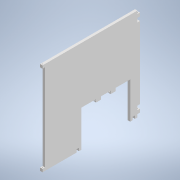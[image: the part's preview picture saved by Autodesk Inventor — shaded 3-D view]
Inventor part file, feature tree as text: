
AUTODESK INVENTOR PART (.ipt)
format: ipt  version: 2020 (Build 240168000, 168)  size: 333,312 bytes
history: native  units: in
note: dims shown in document units (in); Inventor stores cm internally (conversion verified against a paired STEP export)
features: sketch x9, hole x7, extrude x6, shell x1, fillet x1, plane x1, split x1
ambient origin geometry x8: Origin, YZ Plane, XZ Plane, XY Plane, X Axis, Y Axis, Z Axis, Center Point
bodies: Solid1 (feature_tree)
feature tree (26):
  extrude  "Extrusion1"  Depth=7.874in
  shell  "Shell1"  Thickness=7.874in
  extrude  "Extrusion2"  Depth=1.6339in
  sketch  "Sketch3"  dims[d7=6.1024in d8=1.6339in]
  extrude  "Extrusion3"  Depth=1.5748in
  hole  "Hole1"  [1 undecoded]
  fillet  "Fillet2"  Radius=0.8661in
  extrude  "Extrusion4"  Depth=1.1417in
  plane  "Work Plane3"
  split  "Split1"
  extrude  "Extrusion11"  Depth=0.3937in
  hole  "Hole3"  [1 undecoded]
  hole  "Hole4"  [1 undecoded]
  hole  "Hole5"  [1 undecoded]
  hole  "Hole6"  [1 undecoded]
  extrude  "Extrusion12"  Depth=0.3937in
  hole  "Hole7"  [1 undecoded]
  sketch  "Sketch1"  dims[d0=7.874in d1=7.874in d2=7.874in d3=0.0in]
  sketch  "Sketch6"  dims[d9=0.3937in d10=0.0in d12=1.5748in]
  sketch  "Sketch7"  dims[d13=1.5748in d16=3.1496in d19=0.8661in]
  hole  "Hole2"  [1 undecoded]
  sketch  "Sketch8"  dims[d20=0.1575in d22=1.1417in]
  sketch  "Sketch9"  dims[d23=0.3937in d24=0.3937in]
  sketch  "Sketch10"  dims[d25=0.0787in d26=0.0in d27=2.8346in]
  sketch  "Sketch11"  dims[d28=0.9843in d29=0.1575in]
  sketch  "Sketch12"  dims[d30=0.1575in d31=0.1969in d32=0.1969in d33=0.3937in d34=0.3937in d35=0.3937in d36=0.1378in d37=0.2362in d38=0.1575in d39=0.0787in d40=90.0deg d41=0.315in d42=0.8108in d43=0.1181in d45=0.1969in d46=0.0in d64=0.0in d65=0.7874in d66=3.937in d71=0.3937in d72=0.0in d73=0.1969in d74=0.2362in d75=0.1969in d76=0.2362in d77=0.1969in d78=0.2362in d79=0.2756in d80=0.315in d81=0.2362in d82=0.2756in d83=0.315in d84=0.1969in d85=0.1969in d86=0.1969in d87=0.2362in d88=0.1969in d89=0.1969in d90=0.1969in d91=0.2362in d92=0.0787in d93=0.2362in d94=0.1575in d95=0.0787in d96=90.0deg d97=0.315in d98=0.0in d99=0.0984in d100=0.0984in d101=0.0787in d102=0.2362in d103=0.1575in d104=0.0787in d105=90.0deg d106=0.315in d107=0.0in d108=0.0787in d109=0.2362in d110=0.1575in d111=0.0787in d112=90.0deg d113=0.315in d114=0.0in d115=0.0984in d116=0.0984in d117=0.0787in d118=0.2362in d119=0.1575in d120=0.0787in d121=90.0deg d122=0.315in d123=0.0in d124=0.0984in d125=0.0984in d126=1.1811in d127=0.3937in d129=1.1811in d130=0.3937in d131=0.2362in d132=0.0in d133=0.1181in d134=0.0984in d135=0.0984in d136=0.2362in d137=0.1575in d138=0.0787in d139=90.0deg d140=0.315in d141=0.0in d5=0.0394in d6=0.0394in d11=0.5635in d14=0.0025in d15=0.0295in d59=0.0197in d60=0.0344in d61=0.0197in d62=0.0344in d63=0.0344in]
note: 7 required parameter values undecoded (feature->parameter linkage not recoverable at this tier; creation-order binding heuristic only, values carry confidence <= 0.55)
